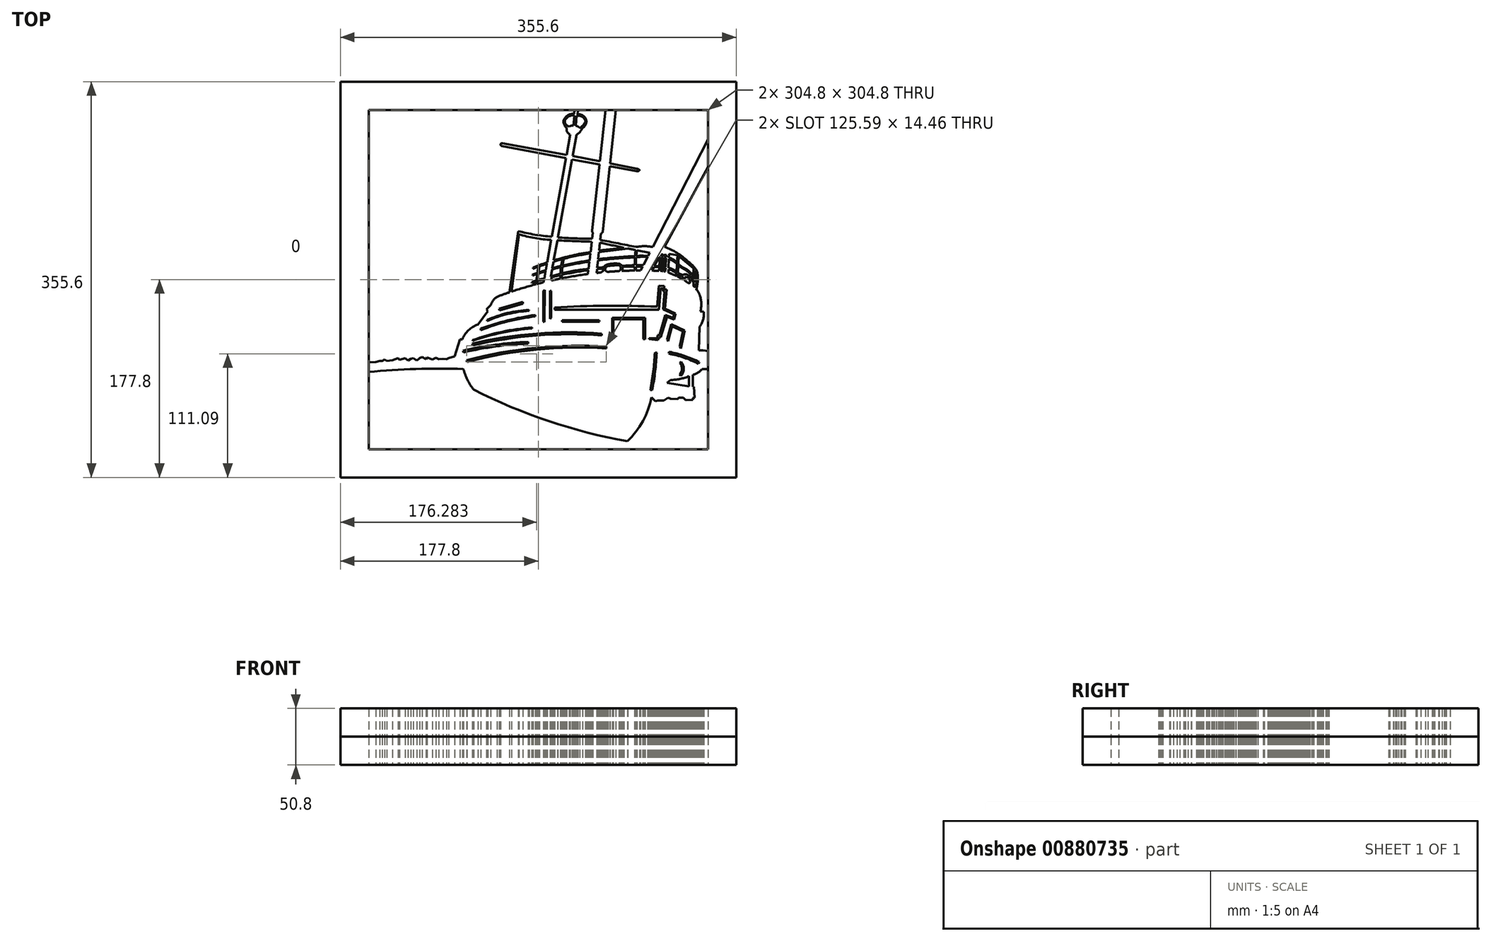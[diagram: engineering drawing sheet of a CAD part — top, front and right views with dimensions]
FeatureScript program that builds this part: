
annotation { "Feature Type Name" : "Feature", "Feature Type Description" : "" }
export const myFeature = defineFeature(function(context is Context, id is Id, definition is map)
    precondition{}
    {
        {
            var Q0;
            Q0=qCreatedBy(makeId("Top.planeOp"),FACE);
            var sketch = newSketch(context, id + "F0", { "sketchPlane" : qUnion([Q0])});
            skLineSegment(sketch, "E0.bottom", {"start": v(0, 0) * mm, "end": v(304.8, 0) * mm});
            skLineSegment(sketch, "E0.top", {"start": v(0, 304.8) * mm, "end": v(304.8, 304.8) * mm});
            skLineSegment(sketch, "E0.left", {"start": v(0, 0) * mm, "end": v(0, 304.8) * mm});
            skLineSegment(sketch, "E0.right", {"start": v(304.8, 0) * mm, "end": v(304.8, 304.8) * mm});
            skArc(sketch, "E1", {"start": v(94.3, 53.56) * mm, "mid": v(161.73, 25.31) * mm, "end": v(232.56, 7.17) * mm});
            skArc(sketch, "E2", {"start": v(85.05, 72.16) * mm, "mid": v(88.82, 62.44) * mm, "end": v(94.3, 53.56) * mm});
            skArc(sketch, "E3", {"start": v(232.56, 7.17) * mm, "mid": v(246.4, 25.26) * mm, "end": v(254.14, 46.67) * mm});
            skLineSegment(sketch, "E4", {"start": v(254.14, 46.67) * mm, "end": v(271.17, 62.17) * mm});
            skArc(sketch, "E5", {"start": v(271.17, 62.17) * mm, "mid": v(279.66, 63.15) * mm, "end": v(287.85, 65.57) * mm});
            skArc(sketch, "E6", {"start": v(290.4, 66.66) * mm, "mid": v(295.48, 68.46) * mm, "end": v(299.52, 72.01) * mm});
            skArc(sketch, "E7", {"start": v(297.32, 110.03) * mm, "mid": v(300.5, 116.32) * mm, "end": v(301.08, 123.34) * mm});
            skArc(sketch, "E8", {"start": v(298.13, 123.68) * mm, "mid": v(298.87, 130.77) * mm, "end": v(297.77, 137.83) * mm});
            skArc(sketch, "E9", {"start": v(297.77, 137.83) * mm, "mid": v(296.7, 140.32) * mm, "end": v(295.27, 142.62) * mm});
            skLineSegment(sketch, "E10", {"start": v(299.52, 72.01) * mm, "end": v(299.52, 79.67) * mm});
            skLineSegment(sketch, "E11", {"start": v(299.52, 79.67) * mm, "end": v(300.6, 88.72) * mm});
            skLineSegment(sketch, "E12", {"start": v(300.6, 88.72) * mm, "end": v(296.73, 88.72) * mm});
            skLineSegment(sketch, "E13", {"start": v(296.73, 88.72) * mm, "end": v(297.32, 110.03) * mm});
            skLineSegment(sketch, "E14", {"start": v(301.08, 123.34) * mm, "end": v(298.13, 123.68) * mm});
            skLineSegment(sketch, "E15", {"start": v(77.34, 83.42) * mm, "end": v(81.94, 98.75) * mm});
            skLineSegment(sketch, "E16", {"start": v(81.94, 98.75) * mm, "end": v(84.22, 98.75) * mm});
            skArc(sketch, "E17", {"start": v(98.1, 112.03) * mm, "mid": v(89.73, 106.89) * mm, "end": v(84.22, 98.75) * mm});
            skLineSegment(sketch, "E18", {"start": v(98.1, 112.03) * mm, "end": v(107.17, 124.2) * mm});
            skLineSegment(sketch, "E19", {"start": v(107.17, 124.2) * mm, "end": v(105.8, 125.59) * mm});
            skLineSegment(sketch, "E20", {"start": v(105.8, 125.59) * mm, "end": v(109.7, 129.49) * mm});
            skArc(sketch, "E21", {"start": v(115.26, 136.92) * mm, "mid": v(111.9, 133.63) * mm, "end": v(109.7, 129.49) * mm});
            skArc(sketch, "E22", {"start": v(265, 160.04) * mm, "mid": v(218.95, 159.65) * mm, "end": v(173.3, 153.51) * mm});
            skArc(sketch, "E23", {"start": v(295.27, 142.62) * mm, "mid": v(281.2, 153.19) * mm, "end": v(265, 160.04) * mm});
            skLineSegment(sketch, "E24", {"start": v(164.3, 151.6) * mm, "end": v(164.3, 154.55) * mm});
            skLineSegment(sketch, "E25", {"start": v(164.3, 154.55) * mm, "end": v(163.51, 154.41) * mm});
            skLineSegment(sketch, "E26", {"start": v(157.8, 153.4) * mm, "end": v(157.06, 149.9) * mm});
            skLineSegment(sketch, "E27", {"start": v(163.51, 154.41) * mm, "end": v(163.62, 155.02) * mm});
            skArc(sketch, "E28", {"start": v(186.7, 282.65) * mm, "mid": v(188.34, 283.6) * mm, "end": v(189.8, 284.83) * mm});
            skArc(sketch, "E29", {"start": v(192.3, 288.71) * mm, "mid": v(195.4, 292.6) * mm, "end": v(194.77, 297.54) * mm});
            skArc(sketch, "E30", {"start": v(194.77, 297.54) * mm, "mid": v(191.72, 300.14) * mm, "end": v(187.83, 301.08) * mm});
            skLineSegment(sketch, "E31", {"start": v(188.16, 304.8) * mm, "end": v(187.83, 301.08) * mm});
            skLineSegment(sketch, "E32", {"start": v(184.75, 301.25) * mm, "end": v(185.1, 304.78) * mm});
            skLineSegment(sketch, "E33", {"start": v(184.1, 290.76) * mm, "end": v(184.92, 299.78) * mm});
            skLineSegment(sketch, "E34", {"start": v(186.1, 290.67) * mm, "end": v(186.92, 299.5) * mm});
            skLineSegment(sketch, "E35", {"start": v(181.18, 282.83) * mm, "end": v(177.88, 264.54) * mm});
            skLineSegment(sketch, "E36", {"start": v(204.79, 158.37) * mm, "end": v(208.84, 193.9) * mm});
            skLineSegment(sketch, "E37", {"start": v(201.6, 194.48) * mm, "end": v(197, 157.43) * mm});
            skLineSegment(sketch, "E38", {"start": v(210.44, 195.17) * mm, "end": v(216.63, 254.16) * mm});
            skLineSegment(sketch, "E39", {"start": v(212.83, 304.8) * mm, "end": v(200.7, 196.5) * mm});
            skArc(sketch, "E40", {"start": v(200.7, 196.5) * mm, "mid": v(200.87, 195.36) * mm, "end": v(201.6, 194.48) * mm});
            skArc(sketch, "E41", {"start": v(208.84, 193.9) * mm, "mid": v(209.71, 194.44) * mm, "end": v(210.44, 195.17) * mm});
            skArc(sketch, "E42", {"start": v(134.37, 196) * mm, "mid": v(149.36, 192.78) * mm, "end": v(164.59, 190.94) * mm});
            skArc(sketch, "E43", {"start": v(135.06, 193.07) * mm, "mid": v(149.41, 189.7) * mm, "end": v(164.07, 188.09) * mm});
            skArc(sketch, "E44", {"start": v(169.98, 190.2) * mm, "mid": v(185.45, 189.43) * mm, "end": v(200.92, 189.03) * mm});
            skArc(sketch, "E45", {"start": v(169.53, 187.72) * mm, "mid": v(185.07, 186.99) * mm, "end": v(200.6, 186.47) * mm});
            skArc(sketch, "E46", {"start": v(208.18, 188.12) * mm, "mid": v(224.23, 184.9) * mm, "end": v(240.3, 181.72) * mm});
            skArc(sketch, "E47", {"start": v(207.88, 185.56) * mm, "mid": v(218.64, 183.28) * mm, "end": v(229.41, 181.06) * mm});
            skLineSegment(sketch, "E48", {"start": v(244.44, 160.58) * mm, "end": v(304.8, 278.4) * mm});
            skLineSegment(sketch, "E49", {"start": v(304.8, 253.65) * mm, "end": v(254.47, 160.46) * mm});
            skLineSegment(sketch, "E50", {"start": v(119.8, 272.39) * mm, "end": v(177.33, 261.5) * mm});
            skLineSegment(sketch, "E51", {"start": v(177.88, 264.54) * mm, "end": v(120.16, 274.96) * mm});
            skLineSegment(sketch, "E52", {"start": v(182.65, 260.3) * mm, "end": v(207.34, 255.83) * mm});
            skLineSegment(sketch, "E53", {"start": v(183.2, 263.37) * mm, "end": v(207.65, 258.6) * mm});
            skArc(sketch, "E54", {"start": v(177.98, 288.57) * mm, "mid": v(178.4, 285.04) * mm, "end": v(181.18, 282.83) * mm});
            skArc(sketch, "E55", {"start": v(189.8, 284.83) * mm, "mid": v(191.13, 286.72) * mm, "end": v(192.3, 288.71) * mm});
            skArc(sketch, "E56", {"start": v(184.92, 299.78) * mm, "mid": v(179.69, 298.94) * mm, "end": v(176.25, 294.92) * mm});
            skArc(sketch, "E57", {"start": v(194.86, 294.45) * mm, "mid": v(191.95, 298.64) * mm, "end": v(186.92, 299.5) * mm});
            skArc(sketch, "E58", {"start": v(189.8, 288.71) * mm, "mid": v(192.76, 291.2) * mm, "end": v(194.86, 294.45) * mm});
            skArc(sketch, "E59", {"start": v(176.25, 294.92) * mm, "mid": v(177.3, 291.63) * mm, "end": v(180.28, 289.9) * mm});
            skArc(sketch, "E60", {"start": v(184.1, 290.76) * mm, "mid": v(182.11, 290.65) * mm, "end": v(180.28, 289.9) * mm});
            skArc(sketch, "E61", {"start": v(189.8, 288.71) * mm, "mid": v(188.07, 289.93) * mm, "end": v(186.1, 290.67) * mm});
            skArc(sketch, "E62", {"start": v(120.16, 274.96) * mm, "mid": v(119.17, 274.8) * mm, "end": v(118.5, 274.06) * mm});
            skArc(sketch, "E63", {"start": v(118.5, 274.06) * mm, "mid": v(118.83, 272.98) * mm, "end": v(119.8, 272.39) * mm});
            skArc(sketch, "E64", {"start": v(243.5, 250.67) * mm, "mid": v(242.29, 251.62) * mm, "end": v(240.83, 252.15) * mm});
            skArc(sketch, "E65", {"start": v(240.69, 249.81) * mm, "mid": v(242.2, 249.9) * mm, "end": v(243.5, 250.67) * mm});
            skArc(sketch, "E66", {"start": v(199.46, 177.22) * mm, "mid": v(182.73, 174.03) * mm, "end": v(166.27, 169.67) * mm});
            skArc(sketch, "E67", {"start": v(199.3, 175.95) * mm, "mid": v(187.26, 173.85) * mm, "end": v(175.35, 171.11) * mm});
            skArc(sketch, "E68", {"start": v(198.51, 169.56) * mm, "mid": v(186.36, 167.57) * mm, "end": v(174.32, 165) * mm});
            skArc(sketch, "E69", {"start": v(198.38, 168.5) * mm, "mid": v(186.23, 166.55) * mm, "end": v(174.19, 164) * mm});
            skArc(sketch, "E70", {"start": v(157.8, 153.4) * mm, "mid": v(154.81, 152.78) * mm, "end": v(151.86, 152) * mm});
            skArc(sketch, "E71", {"start": v(157.6, 152.46) * mm, "mid": v(154.66, 151.92) * mm, "end": v(151.76, 151.15) * mm});
            skArc(sketch, "E72", {"start": v(197.57, 161.96) * mm, "mid": v(185.48, 160.45) * mm, "end": v(173.56, 157.93) * mm});
            skArc(sketch, "E73", {"start": v(197.44, 160.93) * mm, "mid": v(185.42, 159.02) * mm, "end": v(173.47, 156.67) * mm});
            skArc(sketch, "E74", {"start": v(175.35, 171.11) * mm, "mid": v(174.26, 164.55) * mm, "end": v(173.56, 157.93) * mm});
            skArc(sketch, "E75", {"start": v(174.15, 170.8) * mm, "mid": v(172.97, 164.24) * mm, "end": v(172.34, 157.62) * mm});
            skLineSegment(sketch, "E76", {"start": v(207.1, 178.6) * mm, "end": v(229.41, 181.06) * mm});
            skLineSegment(sketch, "E77", {"start": v(232.84, 180.37) * mm, "end": v(206.93, 177.2) * mm});
            skArc(sketch, "E78", {"start": v(239.54, 173.56) * mm, "mid": v(222.85, 172.45) * mm, "end": v(206.2, 170.79) * mm});
            skArc(sketch, "E79", {"start": v(239.13, 172.33) * mm, "mid": v(222.57, 171.35) * mm, "end": v(206.07, 169.65) * mm});
            skArc(sketch, "E80", {"start": v(251.1, 173.56) * mm, "mid": v(245.8, 173.79) * mm, "end": v(240.49, 173.63) * mm});
            skArc(sketch, "E81", {"start": v(250.73, 172.86) * mm, "mid": v(245.55, 172.9) * mm, "end": v(240.39, 172.5) * mm});
            skArc(sketch, "E82", {"start": v(239.92, 178.96) * mm, "mid": v(239.63, 176.26) * mm, "end": v(239.4, 173.56) * mm});
            skArc(sketch, "E83", {"start": v(241.08, 178.6) * mm, "mid": v(240.75, 176.12) * mm, "end": v(240.49, 173.63) * mm});
            skArc(sketch, "E84", {"start": v(227.38, 160.16) * mm, "mid": v(228.04, 163.87) * mm, "end": v(225.37, 166.53) * mm});
            skArc(sketch, "E85", {"start": v(225.37, 166.53) * mm, "mid": v(219.91, 166.77) * mm, "end": v(214.51, 165.95) * mm});
            skArc(sketch, "E86", {"start": v(214.51, 165.95) * mm, "mid": v(211.53, 163.92) * mm, "end": v(210.83, 160.38) * mm});
            skArc(sketch, "E87", {"start": v(212.7, 160.6) * mm, "mid": v(213.91, 159.64) * mm, "end": v(215.44, 159.39) * mm});
            skArc(sketch, "E88", {"start": v(214.95, 164.65) * mm, "mid": v(212.98, 163.1) * mm, "end": v(212.7, 160.6) * mm});
            skArc(sketch, "E89", {"start": v(225.08, 165.3) * mm, "mid": v(220, 165.13) * mm, "end": v(214.95, 164.65) * mm});
            skArc(sketch, "E90", {"start": v(225.08, 160.04) * mm, "mid": v(226.54, 162.67) * mm, "end": v(225.08, 165.3) * mm});
            skArc(sketch, "E91", {"start": v(208.2, 158.73) * mm, "mid": v(209.65, 159.34) * mm, "end": v(210.83, 160.38) * mm});
            skArc(sketch, "E92", {"start": v(210.83, 162.18) * mm, "mid": v(208, 162.17) * mm, "end": v(205.2, 161.9) * mm});
            skArc(sketch, "E93", {"start": v(211.22, 163.37) * mm, "mid": v(208.27, 163.22) * mm, "end": v(205.32, 163) * mm});
            skArc(sketch, "E94", {"start": v(239.06, 165.3) * mm, "mid": v(233.38, 165.04) * mm, "end": v(227.7, 164.65) * mm});
            skArc(sketch, "E95", {"start": v(239.06, 164.25) * mm, "mid": v(233.55, 164.14) * mm, "end": v(228.04, 163.87) * mm});
            skArc(sketch, "E96", {"start": v(255.27, 181.72) * mm, "mid": v(247.78, 182.4) * mm, "end": v(240.3, 181.72) * mm});
            skArc(sketch, "E97", {"start": v(295.37, 159.35) * mm, "mid": v(291.54, 164.64) * mm, "end": v(286.66, 168.96) * mm});
            skArc(sketch, "E98", {"start": v(294.43, 143.41) * mm, "mid": v(295.67, 151.34) * mm, "end": v(295.37, 159.35) * mm});
            skLineSegment(sketch, "E99", {"start": v(240.08, 165.4) * mm, "end": v(247, 165.6) * mm});
            skLineSegment(sketch, "E100", {"start": v(240.08, 164.1) * mm, "end": v(246.25, 164.1) * mm});
            skLineSegment(sketch, "E101", {"start": v(260.92, 160.24) * mm, "end": v(261.62, 172.53) * mm});
            skLineSegment(sketch, "E102", {"start": v(262.22, 160.18) * mm, "end": v(262.93, 172.5) * mm});
            skLineSegment(sketch, "E103", {"start": v(263.06, 174.8) * mm, "end": v(264.68, 175.25) * mm});
            skLineSegment(sketch, "E104", {"start": v(264.68, 175.25) * mm, "end": v(264.18, 160.09) * mm});
            skLineSegment(sketch, "E105", {"start": v(265, 160.04) * mm, "end": v(265.54, 174.62) * mm});
            skLineSegment(sketch, "E106", {"start": v(265.54, 174.62) * mm, "end": v(267.47, 174.55) * mm});
            skLineSegment(sketch, "E107", {"start": v(269.35, 158.65) * mm, "end": v(269.92, 175.49) * mm});
            skLineSegment(sketch, "E108", {"start": v(269.92, 175.49) * mm, "end": v(277.52, 174.4) * mm});
            skLineSegment(sketch, "E109", {"start": v(277.52, 174.4) * mm, "end": v(276.33, 155.75) * mm});
            skLineSegment(sketch, "E110", {"start": v(277.65, 155.1) * mm, "end": v(278.7, 173.55) * mm});
            skLineSegment(sketch, "E111", {"start": v(278.7, 173.55) * mm, "end": v(292.02, 162.47) * mm});
            skLineSegment(sketch, "E112", {"start": v(292.02, 162.47) * mm, "end": v(291.2, 150.99) * mm});
            skLineSegment(sketch, "E113", {"start": v(291.2, 150.99) * mm, "end": v(290.35, 151.05) * mm});
            skLineSegment(sketch, "E114", {"start": v(292.02, 146.61) * mm, "end": v(292.8, 160.42) * mm});
            skLineSegment(sketch, "E115", {"start": v(292.8, 160.42) * mm, "end": v(294.61, 158.05) * mm});
            skLineSegment(sketch, "E116", {"start": v(294.61, 158.05) * mm, "end": v(294.61, 152.4) * mm});
            skLineSegment(sketch, "E117", {"start": v(294.61, 152.4) * mm, "end": v(292.48, 154.95) * mm});
            skLineSegment(sketch, "E118", {"start": v(282.2, 152.6) * mm, "end": v(282.2, 155.15) * mm});
            skLineSegment(sketch, "E119", {"start": v(282.2, 155.15) * mm, "end": v(277.77, 157.25) * mm});
            skLineSegment(sketch, "E120", {"start": v(277.84, 158.44) * mm, "end": v(282.14, 156.42) * mm});
            skLineSegment(sketch, "E121", {"start": v(256.22, 163.7) * mm, "end": v(261.1, 163.42) * mm});
            skLineSegment(sketch, "E122", {"start": v(261.16, 164.33) * mm, "end": v(256.7, 164.58) * mm});
            skLineSegment(sketch, "E123", {"start": v(262.4, 163.3) * mm, "end": v(264.28, 163.24) * mm});
            skLineSegment(sketch, "E124", {"start": v(262.46, 164.31) * mm, "end": v(264.31, 164.25) * mm});
            skLineSegment(sketch, "E125", {"start": v(265.15, 164.1) * mm, "end": v(266.84, 163.74) * mm});
            skLineSegment(sketch, "E126", {"start": v(266.78, 162.74) * mm, "end": v(265.12, 163.14) * mm});
            skLineSegment(sketch, "E127", {"start": v(261.13, 172.8) * mm, "end": v(261.62, 172.53) * mm});
            skLineSegment(sketch, "E128", {"start": v(262.93, 172.5) * mm, "end": v(264.58, 172.4) * mm});
            skLineSegment(sketch, "E129", {"start": v(262.97, 173.3) * mm, "end": v(264.61, 173.25) * mm});
            skLineSegment(sketch, "E130", {"start": v(267.31, 171.78) * mm, "end": v(265.45, 172.21) * mm});
            skLineSegment(sketch, "E131", {"start": v(267.36, 172.57) * mm, "end": v(265.48, 173.04) * mm});
            skLineSegment(sketch, "E132", {"start": v(252.6, 176.52) * mm, "end": v(241.08, 178.6) * mm});
            skArc(sketch, "E133", {"start": v(277.1, 167.84) * mm, "mid": v(273.75, 170.45) * mm, "end": v(269.8, 172.04) * mm});
            skArc(sketch, "E134", {"start": v(277.01, 166.46) * mm, "mid": v(273.63, 169.1) * mm, "end": v(269.77, 170.95) * mm});
            skArc(sketch, "E135", {"start": v(276.55, 159.18) * mm, "mid": v(273.34, 161.65) * mm, "end": v(269.5, 162.91) * mm});
            skArc(sketch, "E136", {"start": v(276.46, 157.85) * mm, "mid": v(273.23, 160.26) * mm, "end": v(269.45, 161.65) * mm});
            skArc(sketch, "E137", {"start": v(285.67, 157.17) * mm, "mid": v(283.85, 157.09) * mm, "end": v(282.14, 156.42) * mm});
            skArc(sketch, "E138", {"start": v(290.1, 153.5) * mm, "mid": v(288.1, 155.6) * mm, "end": v(285.67, 157.17) * mm});
            skArc(sketch, "E139", {"start": v(290.35, 151.05) * mm, "mid": v(290.47, 152.3) * mm, "end": v(290.1, 153.5) * mm});
            skArc(sketch, "E140", {"start": v(288.57, 151.94) * mm, "mid": v(286.83, 154.14) * mm, "end": v(284.06, 154.54) * mm});
            skArc(sketch, "E141", {"start": v(288.57, 149.43) * mm, "mid": v(288.7, 150.69) * mm, "end": v(288.57, 151.94) * mm});
            skArc(sketch, "E142", {"start": v(284.06, 154.54) * mm, "mid": v(283.83, 153) * mm, "end": v(284.06, 151.46) * mm});
            skArc(sketch, "E143", {"start": v(287.06, 149.43) * mm, "mid": v(287.81, 149.3) * mm, "end": v(288.57, 149.43) * mm});
            skArc(sketch, "E144", {"start": v(292.02, 146.61) * mm, "mid": v(292.63, 145.96) * mm, "end": v(293.53, 145.92) * mm});
            skArc(sketch, "E145", {"start": v(293.53, 145.92) * mm, "mid": v(294.27, 148.46) * mm, "end": v(294.38, 151.1) * mm});
            skArc(sketch, "E146", {"start": v(294.38, 151.1) * mm, "mid": v(293.47, 152.23) * mm, "end": v(292.39, 153.19) * mm});
            skArc(sketch, "E147", {"start": v(291.55, 155.97) * mm, "mid": v(287.64, 160.14) * mm, "end": v(282.78, 163.13) * mm});
            skArc(sketch, "E148", {"start": v(291.47, 154.88) * mm, "mid": v(287.42, 159.03) * mm, "end": v(282.62, 162.27) * mm});
            skArc(sketch, "E149", {"start": v(278.25, 165.49) * mm, "mid": v(280.3, 163.7) * mm, "end": v(282.62, 162.27) * mm});
            skArc(sketch, "E150", {"start": v(278.3, 166.52) * mm, "mid": v(280.41, 164.66) * mm, "end": v(282.78, 163.13) * mm});
            skArc(sketch, "E151.trimOffspring", {"start": v(286.66, 168.96) * mm, "mid": v(276.97, 176.42) * mm, "end": v(265.95, 181.72) * mm});
            skArc(sketch, "E152", {"start": v(153.46, 164.32) * mm, "mid": v(153.08, 161.55) * mm, "end": v(152.72, 158.79) * mm});
            skArc(sketch, "E153", {"start": v(150.3, 148.17) * mm, "mid": v(150.48, 149.48) * mm, "end": v(150.66, 150.8) * mm});
            skLineSegment(sketch, "E154", {"start": v(135.06, 193.07) * mm, "end": v(128.56, 141.65) * mm});
            skLineSegment(sketch, "E155", {"start": v(134.37, 196) * mm, "end": v(126.49, 140.95) * mm});
            skLineSegment(sketch, "E156", {"start": v(146.54, 150.1) * mm, "end": v(146.97, 149.3) * mm});
            skLineSegment(sketch, "E157", {"start": v(147.54, 156.1) * mm, "end": v(147.2, 156.86) * mm});
            skLineSegment(sketch, "E158", {"start": v(147.7, 163.23) * mm, "end": v(147.92, 162.22) * mm});
            skPoint(sketch, "E159", {"position": v(180.34, 295.78) * mm});
            skPoint(sketch, "E160", {"position": v(182.6, 295.72) * mm});
            skLineSegment(sketch, "E161", {"start": v(0.01, 78.06) * mm, "end": v(6.4, 78.42) * mm});
            skLineSegment(sketch, "E162", {"start": v(6.4, 78.42) * mm, "end": v(10.04, 79.33) * mm});
            skLineSegment(sketch, "E163", {"start": v(10.04, 79.33) * mm, "end": v(12.22, 79.33) * mm});
            skLineSegment(sketch, "E164", {"start": v(12.22, 79.33) * mm, "end": v(14.41, 80.6) * mm});
            skLineSegment(sketch, "E165", {"start": v(14.41, 80.6) * mm, "end": v(16.42, 79.33) * mm});
            skLineSegment(sketch, "E166", {"start": v(16.42, 79.33) * mm, "end": v(21.34, 79.88) * mm});
            skLineSegment(sketch, "E167", {"start": v(21.34, 79.88) * mm, "end": v(26.44, 81.7) * mm});
            skLineSegment(sketch, "E168", {"start": v(26.44, 81.7) * mm, "end": v(27.72, 80.24) * mm});
            skLineSegment(sketch, "E169", {"start": v(27.72, 80.24) * mm, "end": v(32.82, 81.88) * mm});
            skLineSegment(sketch, "E170", {"start": v(32.82, 81.88) * mm, "end": v(35.56, 79.7) * mm});
            skLineSegment(sketch, "E171", {"start": v(35.56, 79.7) * mm, "end": v(37.93, 81.34) * mm});
            skLineSegment(sketch, "E172", {"start": v(37.93, 81.34) * mm, "end": v(40.11, 81.88) * mm});
            skLineSegment(sketch, "E173", {"start": v(40.11, 81.88) * mm, "end": v(43.21, 79.7) * mm});
            skLineSegment(sketch, "E174", {"start": v(43.21, 79.7) * mm, "end": v(45.95, 81.88) * mm});
            skLineSegment(sketch, "E175", {"start": v(45.95, 81.88) * mm, "end": v(48.14, 82.8) * mm});
            skLineSegment(sketch, "E176", {"start": v(48.14, 82.8) * mm, "end": v(51.6, 80.8) * mm});
            skLineSegment(sketch, "E177", {"start": v(51.6, 80.8) * mm, "end": v(52.7, 82.61) * mm});
            skLineSegment(sketch, "E178", {"start": v(52.7, 82.61) * mm, "end": v(57.25, 80.6) * mm});
            skLineSegment(sketch, "E179", {"start": v(57.25, 80.6) * mm, "end": v(60.53, 82.25) * mm});
            skLineSegment(sketch, "E180", {"start": v(60.53, 82.25) * mm, "end": v(63.08, 80.8) * mm});
            skLineSegment(sketch, "E181", {"start": v(63.08, 80.8) * mm, "end": v(66.73, 81.16) * mm});
            skLineSegment(sketch, "E182", {"start": v(66.73, 81.16) * mm, "end": v(70.01, 80.8) * mm});
            skLineSegment(sketch, "E183", {"start": v(70.01, 80.8) * mm, "end": v(71.83, 81.88) * mm});
            skLineSegment(sketch, "E184", {"start": v(71.83, 81.88) * mm, "end": v(77.34, 83.42) * mm});
            skArc(sketch, "E185", {"start": v(85.05, 72.16) * mm, "mid": v(42.48, 72.07) * mm, "end": v(0, 69.4) * mm});
            skLineSegment(sketch, "E186", {"start": v(300.6, 88.72) * mm, "end": v(304.8, 88.22) * mm});
            skLineSegment(sketch, "E187", {"start": v(299.52, 72.01) * mm, "end": v(304.8, 72.01) * mm});
            skLineSegment(sketch, "E188", {"start": v(268.25, 59.52) * mm, "end": v(287.85, 56.39) * mm});
            skLineSegment(sketch, "E189", {"start": v(287.85, 56.39) * mm, "end": v(287.85, 65.57) * mm});
            skLineSegment(sketch, "E190", {"start": v(291.24, 66.81) * mm, "end": v(291.24, 56.28) * mm});
            skLineSegment(sketch, "E191", {"start": v(291.24, 56.28) * mm, "end": v(292.22, 56.28) * mm});
            skLineSegment(sketch, "E192", {"start": v(292.22, 56.28) * mm, "end": v(292.91, 46.4) * mm});
            skLineSegment(sketch, "E193", {"start": v(292.91, 46.4) * mm, "end": v(291.3, 46.06) * mm});
            skLineSegment(sketch, "E194", {"start": v(291.3, 46.06) * mm, "end": v(291.42, 44.34) * mm});
            skLineSegment(sketch, "E195", {"start": v(291.42, 44.34) * mm, "end": v(285.1, 44) * mm});
            skLineSegment(sketch, "E196", {"start": v(285.1, 44) * mm, "end": v(282.7, 46.18) * mm});
            skLineSegment(sketch, "E197", {"start": v(282.7, 46.18) * mm, "end": v(278.56, 46.3) * mm});
            skLineSegment(sketch, "E198", {"start": v(278.56, 46.3) * mm, "end": v(277.64, 45.14) * mm});
            skLineSegment(sketch, "E199", {"start": v(277.64, 45.14) * mm, "end": v(271.2, 45.49) * mm});
            skLineSegment(sketch, "E200", {"start": v(271.2, 45.49) * mm, "end": v(269.02, 46.3) * mm});
            skLineSegment(sketch, "E201", {"start": v(269.02, 46.3) * mm, "end": v(265.35, 43.76) * mm});
            skLineSegment(sketch, "E202", {"start": v(265.35, 43.76) * mm, "end": v(259.95, 43.65) * mm});
            skLineSegment(sketch, "E203", {"start": v(259.95, 43.65) * mm, "end": v(257.54, 43.07) * mm});
            skLineSegment(sketch, "E204", {"start": v(257.54, 43.07) * mm, "end": v(254.14, 46.67) * mm});
            skArc(sketch, "E205", {"start": v(213.68, 92.21) * mm, "mid": v(150.4, 91.12) * mm, "end": v(88.1, 80.06) * mm});
            skArc(sketch, "E206", {"start": v(254.77, 52.86) * mm, "mid": v(257.4, 69.71) * mm, "end": v(258.82, 86.71) * mm});
            skArc(sketch, "E207", {"start": v(296.43, 76.87) * mm, "mid": v(283.42, 82.24) * mm, "end": v(269.81, 85.85) * mm});
            skLineSegment(sketch, "E208", {"start": v(218.88, 102.92) * mm, "end": v(218.88, 117.96) * mm});
            skLineSegment(sketch, "E209", {"start": v(218.88, 117.96) * mm, "end": v(248.4, 117.96) * mm});
            skLineSegment(sketch, "E210", {"start": v(248.4, 117.96) * mm, "end": v(248.4, 98.58) * mm});
            skLineSegment(sketch, "E211", {"start": v(280.52, 90.47) * mm, "end": v(284, 106.68) * mm});
            skLineSegment(sketch, "E212", {"start": v(284, 106.68) * mm, "end": v(271.84, 112.47) * mm});
            skLineSegment(sketch, "E213", {"start": v(271.84, 112.47) * mm, "end": v(268.08, 98.29) * mm});
            skArc(sketch, "E214", {"start": v(143.36, 94.82) * mm, "mid": v(114.1, 92.27) * mm, "end": v(85.2, 87) * mm});
            skArc(sketch, "E215", {"start": v(294.12, 85.27) * mm, "mid": v(291.4, 86.95) * mm, "end": v(288.27, 87.58) * mm});
            skArc(sketch, "E216", {"start": v(279.31, 67.12) * mm, "mid": v(281.48, 72.3) * mm, "end": v(279.46, 77.53) * mm});
            skArc(sketch, "E217", {"start": v(209.3, 102.23) * mm, "mid": v(151.08, 102.16) * mm, "end": v(93.54, 93.28) * mm});
            skArc(sketch, "E218", {"start": v(259.35, 128.12) * mm, "mid": v(213.24, 128.86) * mm, "end": v(167.14, 127.4) * mm});
            skLineSegment(sketch, "E219", {"start": v(259.35, 128.12) * mm, "end": v(260.97, 146.99) * mm});
            skLineSegment(sketch, "E220", {"start": v(260.97, 146.99) * mm, "end": v(265.59, 146.59) * mm});
            skLineSegment(sketch, "E221", {"start": v(265.59, 146.59) * mm, "end": v(265.6, 143.38) * mm});
            skLineSegment(sketch, "E222", {"start": v(265.6, 143.38) * mm, "end": v(267.7, 143.38) * mm});
            skLineSegment(sketch, "E223", {"start": v(267.7, 143.38) * mm, "end": v(266.33, 126.33) * mm});
            skLineSegment(sketch, "E224", {"start": v(217.43, 129.02) * mm, "end": v(217.43, 130.46) * mm});
            skLineSegment(sketch, "E225", {"start": v(217.43, 130.46) * mm, "end": v(193.85, 132.63) * mm});
            skLineSegment(sketch, "E226", {"start": v(193.85, 132.63) * mm, "end": v(192.54, 130.6) * mm});
            skLineSegment(sketch, "E227", {"start": v(192.54, 130.6) * mm, "end": v(194.28, 128.58) * mm});
            skLineSegment(sketch, "E228", {"start": v(156.95, 114.55) * mm, "end": v(156.95, 142.18) * mm});
            skLineSegment(sketch, "E229", {"start": v(163.9, 142.18) * mm, "end": v(163.9, 118.16) * mm});
            skLineSegment(sketch, "E230", {"start": v(218.88, 102.92) * mm, "end": v(219.94, 102.5) * mm});
            skLineSegment(sketch, "E231", {"start": v(219.94, 102.5) * mm, "end": v(219.94, 116.82) * mm});
            skLineSegment(sketch, "E232", {"start": v(219.94, 116.82) * mm, "end": v(246.94, 116.55) * mm});
            skLineSegment(sketch, "E233", {"start": v(246.94, 116.55) * mm, "end": v(246.94, 98.87) * mm});
            skLineSegment(sketch, "E234", {"start": v(246.94, 98.87) * mm, "end": v(248.4, 98.58) * mm});
            skLineSegment(sketch, "E235", {"start": v(268.08, 98.29) * mm, "end": v(268.94, 97.2) * mm});
            skLineSegment(sketch, "E236", {"start": v(268.94, 97.2) * mm, "end": v(272.49, 110.58) * mm});
            skLineSegment(sketch, "E237", {"start": v(272.49, 110.58) * mm, "end": v(282.3, 105.9) * mm});
            skLineSegment(sketch, "E238", {"start": v(282.3, 105.9) * mm, "end": v(279.56, 92.44) * mm});
            skLineSegment(sketch, "E239", {"start": v(279.56, 92.44) * mm, "end": v(280.52, 90.47) * mm});
            skArc(sketch, "E240.0", {"start": v(213.57, 90.56) * mm, "mid": v(150.56, 89.48) * mm, "end": v(88.5, 78.46) * mm});
            skArc(sketch, "E241.0", {"start": v(209.42, 103.88) * mm, "mid": v(150.95, 103.8) * mm, "end": v(93.17, 94.88) * mm});
            skArc(sketch, "E242.0", {"start": v(297.16, 78.36) * mm, "mid": v(283.95, 83.8) * mm, "end": v(270.13, 87.47) * mm});
            skArc(sketch, "E243.0", {"start": v(280.49, 65.96) * mm, "mid": v(283.13, 72.27) * mm, "end": v(280.66, 78.66) * mm});
            skArc(sketch, "E244.0", {"start": v(143.3, 96.47) * mm, "mid": v(113.88, 93.9) * mm, "end": v(84.83, 88.61) * mm});
            skLineSegment(sketch, "E245", {"start": v(143.36, 94.82) * mm, "end": v(143.3, 96.47) * mm});
            skLineSegment(sketch, "E246", {"start": v(93.54, 93.28) * mm, "end": v(93.17, 94.88) * mm});
            skLineSegment(sketch, "E247", {"start": v(85.2, 87) * mm, "end": v(84.83, 88.61) * mm});
            skLineSegment(sketch, "E248", {"start": v(88.5, 78.46) * mm, "end": v(88.1, 80.06) * mm});
            skLineSegment(sketch, "E249", {"start": v(213.57, 90.56) * mm, "end": v(213.68, 92.21) * mm});
            skLineSegment(sketch, "E250", {"start": v(209.3, 102.23) * mm, "end": v(209.42, 103.88) * mm});
            skLineSegment(sketch, "E251", {"start": v(269.81, 85.85) * mm, "end": v(270.13, 87.47) * mm});
            skLineSegment(sketch, "E252", {"start": v(296.43, 76.87) * mm, "end": v(297.16, 78.36) * mm});
            skLineSegment(sketch, "E253", {"start": v(279.46, 77.53) * mm, "end": v(280.66, 78.66) * mm});
            skLineSegment(sketch, "E254", {"start": v(279.31, 67.12) * mm, "end": v(280.49, 65.96) * mm});
            skArc(sketch, "E255.0", {"start": v(253.14, 53.17) * mm, "mid": v(255.77, 69.9) * mm, "end": v(257.17, 86.79) * mm});
            skLineSegment(sketch, "E256", {"start": v(258.82, 86.71) * mm, "end": v(257.17, 86.79) * mm});
            skLineSegment(sketch, "E257", {"start": v(254.77, 52.86) * mm, "end": v(253.14, 53.17) * mm});
            skLineSegment(sketch, "E258", {"start": v(252, 99.01) * mm, "end": v(259.7, 98.04) * mm});
            skLineSegment(sketch, "E259", {"start": v(259.7, 98.04) * mm, "end": v(261.07, 100.62) * mm});
            skLineSegment(sketch, "E260", {"start": v(261.07, 100.62) * mm, "end": v(262.56, 100.5) * mm});
            skLineSegment(sketch, "E261", {"start": v(262.56, 100.5) * mm, "end": v(268.19, 118.88) * mm});
            skLineSegment(sketch, "E262", {"start": v(268.19, 118.88) * mm, "end": v(274.62, 116.55) * mm});
            skLineSegment(sketch, "E263", {"start": v(274.62, 116.55) * mm, "end": v(275.77, 121.98) * mm});
            skLineSegment(sketch, "E264", {"start": v(275.77, 121.98) * mm, "end": v(266.33, 126.33) * mm});
            skLineSegment(sketch, "E265", {"start": v(138.65, 132.2) * mm, "end": v(117.3, 126.33) * mm});
            skLineSegment(sketch, "E266", {"start": v(117.3, 126.33) * mm, "end": v(117.7, 124.86) * mm});
            skLineSegment(sketch, "E267", {"start": v(117.7, 124.86) * mm, "end": v(138.65, 130.62) * mm});
            skLineSegment(sketch, "E268", {"start": v(138.65, 130.62) * mm, "end": v(138.65, 132.2) * mm});
            skLineSegment(sketch, "E269", {"start": v(167.14, 127.4) * mm, "end": v(167.14, 125.5) * mm});
            skLineSegment(sketch, "E270", {"start": v(167.14, 125.5) * mm, "end": v(260.97, 125.5) * mm});
            skLineSegment(sketch, "E271", {"start": v(260.97, 125.5) * mm, "end": v(262.42, 144.75) * mm});
            skLineSegment(sketch, "E272", {"start": v(262.42, 144.75) * mm, "end": v(264.44, 144.46) * mm});
            skLineSegment(sketch, "E273", {"start": v(264.44, 144.46) * mm, "end": v(264.59, 141.71) * mm});
            skLineSegment(sketch, "E274", {"start": v(264.59, 141.71) * mm, "end": v(265.89, 141.71) * mm});
            skLineSegment(sketch, "E275", {"start": v(265.89, 141.71) * mm, "end": v(264.73, 125.65) * mm});
            skLineSegment(sketch, "E276", {"start": v(264.73, 125.65) * mm, "end": v(274.42, 121.17) * mm});
            skLineSegment(sketch, "E277", {"start": v(274.42, 121.17) * mm, "end": v(273.56, 118.13) * mm});
            skLineSegment(sketch, "E278", {"start": v(273.56, 118.13) * mm, "end": v(266.47, 120.73) * mm});
            skLineSegment(sketch, "E279", {"start": v(266.47, 120.73) * mm, "end": v(261.55, 102.94) * mm});
            skLineSegment(sketch, "E280", {"start": v(261.55, 102.94) * mm, "end": v(259.96, 102.36) * mm});
            skLineSegment(sketch, "E281", {"start": v(259.96, 102.36) * mm, "end": v(259.23, 99.76) * mm});
            skLineSegment(sketch, "E282", {"start": v(259.23, 99.76) * mm, "end": v(252, 99.76) * mm});
            skLineSegment(sketch, "E283", {"start": v(252, 99.76) * mm, "end": v(252, 99.01) * mm});
            skLineSegment(sketch, "E284", {"start": v(173.87, 115.82) * mm, "end": v(207.3, 115.82) * mm});
            skLineSegment(sketch, "E285", {"start": v(207.3, 115.82) * mm, "end": v(207.36, 114.59) * mm});
            skLineSegment(sketch, "E286", {"start": v(207.36, 114.59) * mm, "end": v(173.87, 114.51) * mm});
            skLineSegment(sketch, "E287", {"start": v(173.87, 114.51) * mm, "end": v(173.87, 115.82) * mm});
            skArc(sketch, "E288", {"start": v(149.8, 120.57) * mm, "mid": v(125.03, 115.8) * mm, "end": v(100.9, 108.41) * mm});
            skArc(sketch, "E289", {"start": v(146.91, 109.42) * mm, "mid": v(119.84, 105.47) * mm, "end": v(93.52, 98) * mm});
            skArc(sketch, "E290", {"start": v(144.02, 125.2) * mm, "mid": v(124.87, 122.34) * mm, "end": v(106.54, 116.08) * mm});
            skArc(sketch, "E291", {"start": v(149.8, 119.28) * mm, "mid": v(124.95, 114.78) * mm, "end": v(100.9, 107.05) * mm});
            skArc(sketch, "E292", {"start": v(146.91, 108.41) * mm, "mid": v(119.88, 104.77) * mm, "end": v(93.62, 97.42) * mm});
            skLineSegment(sketch, "E293", {"start": v(93.62, 97.42) * mm, "end": v(93.52, 98) * mm});
            skLineSegment(sketch, "E294", {"start": v(100.9, 107.05) * mm, "end": v(100.9, 108.41) * mm});
            skLineSegment(sketch, "E295", {"start": v(146.91, 108.41) * mm, "end": v(146.91, 109.42) * mm});
            skLineSegment(sketch, "E296", {"start": v(149.8, 119.28) * mm, "end": v(149.8, 120.57) * mm});
            skArc(sketch, "E297", {"start": v(144.2, 124.25) * mm, "mid": v(124.9, 121.46) * mm, "end": v(106.44, 115.2) * mm});
            skLineSegment(sketch, "E298", {"start": v(106.44, 115.2) * mm, "end": v(106.54, 116.08) * mm});
            skLineSegment(sketch, "E299", {"start": v(144.2, 124.25) * mm, "end": v(144.02, 125.2) * mm});
            skLineSegment(sketch, "E300", {"start": v(156.95, 114.55) * mm, "end": v(157.98, 114.36) * mm});
            skLineSegment(sketch, "E301", {"start": v(157.98, 114.36) * mm, "end": v(158.13, 143.02) * mm});
            skLineSegment(sketch, "E302", {"start": v(158.13, 143.02) * mm, "end": v(156.95, 142.18) * mm});
            skLineSegment(sketch, "E303", {"start": v(163.9, 142.18) * mm, "end": v(162.97, 142.35) * mm});
            skLineSegment(sketch, "E304", {"start": v(162.97, 142.35) * mm, "end": v(162.97, 117.04) * mm});
            skLineSegment(sketch, "E305", {"start": v(162.97, 117.04) * mm, "end": v(163.9, 118.16) * mm});
            skLineSegment(sketch, "E306.bottom", {"start": v(-25.4, 330.2) * mm, "end": v(330.2, 330.2) * mm});
            skLineSegment(sketch, "E306.top", {"start": v(-25.4, -25.4) * mm, "end": v(330.2, -25.4) * mm});
            skLineSegment(sketch, "E306.left", {"start": v(-25.4, 330.2) * mm, "end": v(-25.4, -25.4) * mm});
            skLineSegment(sketch, "E306.right", {"start": v(330.2, 330.2) * mm, "end": v(330.2, -25.4) * mm});
            skArc(sketch, "E307.trimOffspring", {"start": v(157.06, 149.9) * mm, "mid": v(154.25, 149.2) * mm, "end": v(151.43, 148.47) * mm});
            skArc(sketch, "E308.trimOffspring", {"start": v(158.98, 159.89) * mm, "mid": v(155.78, 158.9) * mm, "end": v(152.6, 157.86) * mm});
            skArc(sketch, "E309.trimOffspring", {"start": v(159.15, 160.85) * mm, "mid": v(155.93, 159.84) * mm, "end": v(152.72, 158.79) * mm});
            skArc(sketch, "E310.trimOffspring", {"start": v(160.2, 166.66) * mm, "mid": v(156.82, 165.52) * mm, "end": v(153.46, 164.32) * mm});
            skArc(sketch, "E311.trimOffspring", {"start": v(160.4, 167.82) * mm, "mid": v(154.02, 165.61) * mm, "end": v(147.7, 163.23) * mm});
            skArc(sketch, "E312.trimOffspring", {"start": v(152.4, 163.93) * mm, "mid": v(150.16, 163.08) * mm, "end": v(147.92, 162.22) * mm});
            skArc(sketch, "E313.trimOffspring", {"start": v(151.68, 158.44) * mm, "mid": v(149.43, 157.66) * mm, "end": v(147.2, 156.86) * mm});
            skArc(sketch, "E314.trimOffspring", {"start": v(151.56, 157.5) * mm, "mid": v(149.54, 156.82) * mm, "end": v(147.54, 156.1) * mm});
            skArc(sketch, "E315.trimOffspring", {"start": v(152.6, 157.86) * mm, "mid": v(152.22, 154.93) * mm, "end": v(151.86, 152) * mm});
            skArc(sketch, "E316.trimOffspring", {"start": v(151.68, 158.44) * mm, "mid": v(152.04, 161.18) * mm, "end": v(152.4, 163.93) * mm});
            skArc(sketch, "E317.trimOffspring", {"start": v(151.76, 151.15) * mm, "mid": v(151.6, 149.8) * mm, "end": v(151.43, 148.47) * mm});
            skArc(sketch, "E318.trimOffspring", {"start": v(150.78, 151.66) * mm, "mid": v(148.64, 150.93) * mm, "end": v(146.54, 150.1) * mm});
            skArc(sketch, "E319.trimOffspring", {"start": v(150.78, 151.66) * mm, "mid": v(151.17, 154.58) * mm, "end": v(151.56, 157.5) * mm});
            skArc(sketch, "E320.trimOffspring", {"start": v(150.66, 150.8) * mm, "mid": v(148.8, 150.1) * mm, "end": v(146.97, 149.3) * mm});
            skArc(sketch, "E321.trimOffspring", {"start": v(150.3, 148.17) * mm, "mid": v(132.64, 142.98) * mm, "end": v(115.26, 136.92) * mm});
            skLineSegment(sketch, "E322.trimOffspring", {"start": v(164.99, 162.57) * mm, "end": v(169.53, 187.72) * mm});
            skArc(sketch, "E323.trimOffspring", {"start": v(174.15, 170.8) * mm, "mid": v(170.1, 169.7) * mm, "end": v(166.06, 168.52) * mm});
            skArc(sketch, "E324.trimOffspring", {"start": v(173.03, 164.68) * mm, "mid": v(169, 163.66) * mm, "end": v(164.99, 162.57) * mm});
            skArc(sketch, "E325.trimOffspring", {"start": v(172.9, 163.69) * mm, "mid": v(168.85, 162.67) * mm, "end": v(164.8, 161.58) * mm});
            skArc(sketch, "E326.trimOffspring", {"start": v(172.34, 157.62) * mm, "mid": v(167.96, 156.39) * mm, "end": v(163.62, 155.02) * mm});
            skArc(sketch, "E327.trimOffspring", {"start": v(172.29, 156.41) * mm, "mid": v(168.29, 155.5) * mm, "end": v(164.3, 154.55) * mm});
            skArc(sketch, "E328.trimOffspring", {"start": v(173.47, 156.67) * mm, "mid": v(173.38, 155.1) * mm, "end": v(173.3, 153.51) * mm});
            skArc(sketch, "E329.trimOffspring", {"start": v(172.29, 156.41) * mm, "mid": v(172.24, 154.85) * mm, "end": v(172.23, 153.3) * mm});
            skArc(sketch, "E330.trimOffspring", {"start": v(172.23, 153.3) * mm, "mid": v(168.26, 152.47) * mm, "end": v(164.3, 151.6) * mm});
            skLineSegment(sketch, "E331", {"start": v(164.8, 161.58) * mm, "end": v(163.62, 155.02) * mm});
            skArc(sketch, "E332.trimOffspring", {"start": v(232.84, 180.37) * mm, "mid": v(236.35, 179.67) * mm, "end": v(239.86, 178.97) * mm});
            skPoint(sketch, "E333.orphan", {"position": v(241.6, 181.72) * mm});
            skArc(sketch, "E334.extension", {"start": v(239.86, 178.97) * mm, "mid": v(239.9, 178.97) * mm, "end": v(239.92, 178.96) * mm});
            skArc(sketch, "E335.trimOffspring", {"start": v(240.39, 172.5) * mm, "mid": v(240.1, 166.53) * mm, "end": v(240.18, 160.55) * mm});
            skArc(sketch, "E336.trimOffspring", {"start": v(239.31, 172.36) * mm, "mid": v(239.07, 166.45) * mm, "end": v(239.13, 160.53) * mm});
            skArc(sketch, "E337.trimOffspring", {"start": v(239.31, 172.36) * mm, "mid": v(239.22, 172.34) * mm, "end": v(239.13, 172.33) * mm});
            skLineSegment(sketch, "E338.trimOffspring", {"start": v(262.97, 173.3) * mm, "end": v(263.06, 174.8) * mm});
            skLineSegment(sketch, "E339.trimOffspring", {"start": v(267.31, 171.78) * mm, "end": v(266.84, 163.74) * mm});
            skLineSegment(sketch, "E340.trimOffspring", {"start": v(266.78, 162.74) * mm, "end": v(266.6, 159.57) * mm});
            skLineSegment(sketch, "E341.trimOffspring", {"start": v(216.63, 254.16) * mm, "end": v(240.69, 249.81) * mm});
            skLineSegment(sketch, "E342.trimOffspring", {"start": v(216.9, 256.8) * mm, "end": v(240.83, 252.15) * mm});
            skLineSegment(sketch, "E343.trimOffspring", {"start": v(216.9, 256.8) * mm, "end": v(221.94, 304.8) * mm});
            skPoint(sketch, "E344.orphan", {"position": v(186.7, 301) * mm});
            skLineSegment(sketch, "E345.trimOffspring", {"start": v(183.2, 263.37) * mm, "end": v(186.7, 282.65) * mm});
            skLineSegment(sketch, "E346.trimOffspring", {"start": v(177.33, 261.5) * mm, "end": v(164.59, 190.94) * mm});
            skLineSegment(sketch, "E347.trimOffspring", {"start": v(164.07, 188.09) * mm, "end": v(157.8, 153.4) * mm});
            skLineSegment(sketch, "E348.trimOffspring", {"start": v(169.98, 190.2) * mm, "end": v(182.65, 260.3) * mm});
            skLineSegment(sketch, "E349", {"start": v(185.1, 304.78) * mm, "end": v(188.16, 304.8) * mm});
            skLineSegment(sketch, "E350", {"start": v(212.83, 304.8) * mm, "end": v(221.94, 304.8) * mm});
            skLineSegment(sketch, "E351", {"start": v(0, 69.4) * mm, "end": v(0.01, 78.06) * mm});
            skLineSegment(sketch, "E352", {"start": v(304.8, 72.01) * mm, "end": v(304.8, 88.22) * mm});
            skLineSegment(sketch, "E353", {"start": v(304.8, 253.65) * mm, "end": v(304.8, 278.4) * mm});
            skLineSegment(sketch, "E354.bottom", {"start": v(304.8, 304.8) * mm, "end": v(0, 304.8) * mm});
            skLineSegment(sketch, "E354.top", {"start": v(304.8, 0) * mm, "end": v(0, 0) * mm});
            skLineSegment(sketch, "E354.left", {"start": v(304.8, 304.8) * mm, "end": v(304.8, 0) * mm});
            skLineSegment(sketch, "E354.right", {"start": v(0, 304.8) * mm, "end": v(0, 0) * mm});
            skLineSegment(sketch, "E355", {"start": v(267.36, 172.57) * mm, "end": v(267.47, 174.55) * mm});
            skArc(sketch, "E356", {"start": v(175.1, 295.1) * mm, "mid": v(175.8, 291.51) * mm, "end": v(177.98, 288.57) * mm});
            skArc(sketch, "E357", {"start": v(184.76, 301.26) * mm, "mid": v(178.85, 299.87) * mm, "end": v(175.1, 295.1) * mm});
            skSolve(sketch);
        }
        {
            var Q0;
            Q0=makeQuery(id+"F0.imprint","IMPRINT",FACE,{"disambiguationData":[TD([[makeQuery(id+"F0.imprint","IMPRINT",EDGE,{"derivedFrom":sQuery(id+"F0.wireOp",EDGE,"E1")}),1.0]])]});
            var Q1;
            {var subQ3=sQuery(id+"F0.wireOp",EDGE,"E48");var subQ4=sQuery(id+"F0.wireOp",EDGE,"E22");var subQ5=makeQuery(id+"F0.imprint","INTERSECT",VERTEX,{"derivedFrom":[subQ4,subQ3]});Q1=makeQuery(id+"F0.imprint","IMPRINT",FACE,{"disambiguationData":[TD([[makeQuery(id+"F0.imprint","IMPRINT",EDGE,{"disambiguationData":[TD([[subQ5,1.0]])],"derivedFrom":subQ4}),-1.0]])]});}
            var Q2;
            {var subQ19=sQuery(id+"F0.wireOp",EDGE,"E46");Q2=makeQuery(id+"F0.imprint","IMPRINT",FACE,{"disambiguationData":[TD([[makeQuery(id+"F0.imprint","IMPRINT",EDGE,{"derivedFrom":subQ19}),-1.0]])]});}
            var Q3;
            Q3=makeQuery(id+"F0.imprint","IMPRINT",FACE,{"disambiguationData":[TD([[makeQuery(id+"F0.imprint","IMPRINT",EDGE,{"derivedFrom":sQuery(id+"F0.wireOp",EDGE,"E38")}),1.0]])]});
            var Q4;
            {var subQ0=sQuery(id+"F0.wireOp",EDGE,"E68");Q4=makeQuery(id+"F0.imprint","IMPRINT",FACE,{"disambiguationData":[TD([[makeQuery(id+"F0.imprint","IMPRINT",EDGE,{"derivedFrom":subQ0}),1.0]])]});}
            var Q5;
            {var subQ0=sQuery(id+"F0.wireOp",EDGE,"E92");Q5=makeQuery(id+"F0.imprint","IMPRINT",FACE,{"disambiguationData":[TD([[makeQuery(id+"F0.imprint","IMPRINT",EDGE,{"derivedFrom":subQ0}),-1.0]])]});}
            var Q6;
            {var subQ7=sQuery(id+"F0.wireOp",EDGE,"E85");Q6=makeQuery(id+"F0.imprint","IMPRINT",FACE,{"disambiguationData":[TD([[makeQuery(id+"F0.imprint","IMPRINT",EDGE,{"derivedFrom":subQ7}),1.0]])]});}
            var Q7;
            {var subQ0=sQuery(id+"F0.wireOp",EDGE,"E94");Q7=makeQuery(id+"F0.imprint","IMPRINT",FACE,{"disambiguationData":[TD([[makeQuery(id+"F0.imprint","IMPRINT",EDGE,{"derivedFrom":subQ0}),1.0]])]});}
            var Q8;
            {var subQ0=sQuery(id+"F0.wireOp",EDGE,"E99");Q8=makeQuery(id+"F0.imprint","IMPRINT",FACE,{"disambiguationData":[TD([[makeQuery(id+"F0.imprint","IMPRINT",EDGE,{"derivedFrom":subQ0}),-1.0]])]});}
            var Q9;
            {var subQ0=sQuery(id+"F0.wireOp",EDGE,"E121");Q9=makeQuery(id+"F0.imprint","IMPRINT",FACE,{"disambiguationData":[TD([[makeQuery(id+"F0.imprint","IMPRINT",EDGE,{"derivedFrom":subQ0}),1.0]])]});}
            var Q10;
            Q10=makeQuery(id+"F0.imprint","IMPRINT",FACE,{"disambiguationData":[TD([[makeQuery(id+"F0.imprint","IMPRINT",EDGE,{"derivedFrom":sQuery(id+"F0.wireOp",EDGE,"E97")}),1.0]])]});
            var Q11;
            {var subQ0=sQuery(id+"F0.wireOp",EDGE,"E135");Q11=makeQuery(id+"F0.imprint","IMPRINT",FACE,{"disambiguationData":[TD([[makeQuery(id+"F0.imprint","IMPRINT",EDGE,{"derivedFrom":subQ0}),1.0]])]});}
            var Q12;
            {var subQ0=sQuery(id+"F0.wireOp",EDGE,"E133");Q12=makeQuery(id+"F0.imprint","IMPRINT",FACE,{"disambiguationData":[TD([[makeQuery(id+"F0.imprint","IMPRINT",EDGE,{"derivedFrom":subQ0}),1.0]])]});}
            var Q13;
            {var subQ1=sQuery(id+"F0.wireOp",EDGE,"E147");Q13=makeQuery(id+"F0.imprint","IMPRINT",FACE,{"disambiguationData":[TD([[makeQuery(id+"F0.imprint","IMPRINT",EDGE,{"derivedFrom":subQ1}),1.0]])]});}
            var Q14;
            Q14=makeQuery(id+"F0.imprint","IMPRINT",FACE,{"disambiguationData":[TD([[makeQuery(id+"F0.imprint","IMPRINT",EDGE,{"derivedFrom":sQuery(id+"F0.wireOp",EDGE,"E10")}),-1.0]])]});
            extrude(context, id + "F1", {"entities" : qUnion([Q0, Q1, Q2, Q3, Q4, Q5, Q6, Q7, Q8, Q9, Q10, Q11, Q12, Q13, Q14]), "depth" : 25.4 * mm, "offsetDistance" : 25.4 * mm});
        }
        {
            var Q0;
            Q0=qCreatedBy(makeId("Top.planeOp"),FACE);
            var sketch = newSketch(context, id + "F2", { "sketchPlane" : qUnion([Q0])});
            skLineSegment(sketch, "E358.bottom", {"start": v(0, 0) * mm, "end": v(304.8, 0) * mm});
            skLineSegment(sketch, "E358.top", {"start": v(0, 304.8) * mm, "end": v(304.8, 304.8) * mm});
            skLineSegment(sketch, "E358.left", {"start": v(0, 0) * mm, "end": v(0, 304.8) * mm});
            skLineSegment(sketch, "E358.right", {"start": v(304.8, 0) * mm, "end": v(304.8, 304.8) * mm});
            skLineSegment(sketch, "E359.0", {"start": v(-25.4, 330.2) * mm, "end": v(330.2, 330.2) * mm});
            skLineSegment(sketch, "E359.1", {"start": v(-25.4, -25.4) * mm, "end": v(-25.4, 330.2) * mm});
            skLineSegment(sketch, "E359.2", {"start": v(-25.4, -25.4) * mm, "end": v(330.2, -25.4) * mm});
            skLineSegment(sketch, "E359.3", {"start": v(330.2, -25.4) * mm, "end": v(330.2, 330.2) * mm});
            skSolve(sketch);
        }
        {
            var Q0;
            Q0=makeQuery(id+"F2.imprint","IMPRINT",FACE,{"disambiguationData":[TD([[makeQuery(id+"F2.imprint","IMPRINT",EDGE,{"derivedFrom":sQuery(id+"F2.wireOp",EDGE,"E358.bottom")}),-1.0]])]});
            extrude(context, id + "F3", {"entities" : qUnion([Q0]), "depth" : 25.4 * mm, "offsetDistance" : 25.4 * mm});
        }
        {
            var Q0;
            Q0=makeQuery(id+"F1.opExtrude","CAP_FACE",FACE,{"disambiguationData":[OSD([sQuery(id+"F0.wireOp",EDGE,"E1"),sQuery(id+"F0.wireOp",EDGE,"E2"),sQuery(id+"F0.wireOp",EDGE,"E3"),sQuery(id+"F0.wireOp",EDGE,"E4"),sQuery(id+"F0.wireOp",EDGE,"E5"),sQuery(id+"F0.wireOp",EDGE,"E6"),sQuery(id+"F0.wireOp",EDGE,"E7"),sQuery(id+"F0.wireOp",EDGE,"E8"),sQuery(id+"F0.wireOp",EDGE,"E9"),sQuery(id+"F0.wireOp",EDGE,"E12"),sQuery(id+"F0.wireOp",EDGE,"E13"),sQuery(id+"F0.wireOp",EDGE,"E14"),sQuery(id+"F0.wireOp",EDGE,"E15"),sQuery(id+"F0.wireOp",EDGE,"E16"),sQuery(id+"F0.wireOp",EDGE,"E17"),sQuery(id+"F0.wireOp",EDGE,"E18"),sQuery(id+"F0.wireOp",EDGE,"E19"),sQuery(id+"F0.wireOp",EDGE,"E20"),sQuery(id+"F0.wireOp",EDGE,"E21"),sQuery(id+"F0.wireOp",EDGE,"E22"),sQuery(id+"F0.wireOp",EDGE,"E23"),sQuery(id+"F0.wireOp",EDGE,"E24"),sQuery(id+"F0.wireOp",EDGE,"E26"),sQuery(id+"F0.wireOp",EDGE,"E28"),sQuery(id+"F0.wireOp",EDGE,"E29"),sQuery(id+"F0.wireOp",EDGE,"E30"),sQuery(id+"F0.wireOp",EDGE,"E31"),sQuery(id+"F0.wireOp",EDGE,"E32"),sQuery(id+"F0.wireOp",EDGE,"E33"),sQuery(id+"F0.wireOp",EDGE,"E34"),sQuery(id+"F0.wireOp",EDGE,"E35"),sQuery(id+"F0.wireOp",EDGE,"E36"),sQuery(id+"F0.wireOp",EDGE,"E37"),sQuery(id+"F0.wireOp",EDGE,"E38"),sQuery(id+"F0.wireOp",EDGE,"E39"),sQuery(id+"F0.wireOp",EDGE,"E40"),sQuery(id+"F0.wireOp",EDGE,"E41"),sQuery(id+"F0.wireOp",EDGE,"E42"),sQuery(id+"F0.wireOp",EDGE,"E43"),sQuery(id+"F0.wireOp",EDGE,"E44"),sQuery(id+"F0.wireOp",EDGE,"E45"),sQuery(id+"F0.wireOp",EDGE,"E46"),sQuery(id+"F0.wireOp",EDGE,"E47"),sQuery(id+"F0.wireOp",EDGE,"E48"),sQuery(id+"F0.wireOp",EDGE,"E49"),sQuery(id+"F0.wireOp",EDGE,"E50"),sQuery(id+"F0.wireOp",EDGE,"E51"),sQuery(id+"F0.wireOp",EDGE,"E52"),sQuery(id+"F0.wireOp",EDGE,"E53"),sQuery(id+"F0.wireOp",EDGE,"E54"),sQuery(id+"F0.wireOp",EDGE,"E55"),sQuery(id+"F0.wireOp",EDGE,"E56"),sQuery(id+"F0.wireOp",EDGE,"E57"),sQuery(id+"F0.wireOp",EDGE,"E58"),sQuery(id+"F0.wireOp",EDGE,"E59"),sQuery(id+"F0.wireOp",EDGE,"E60"),sQuery(id+"F0.wireOp",EDGE,"E61"),sQuery(id+"F0.wireOp",EDGE,"E62"),sQuery(id+"F0.wireOp",EDGE,"E63"),sQuery(id+"F0.wireOp",EDGE,"E64"),sQuery(id+"F0.wireOp",EDGE,"E65"),sQuery(id+"F0.wireOp",EDGE,"E66"),sQuery(id+"F0.wireOp",EDGE,"E67"),sQuery(id+"F0.wireOp",EDGE,"E68"),sQuery(id+"F0.wireOp",EDGE,"E69"),sQuery(id+"F0.wireOp",EDGE,"E70"),sQuery(id+"F0.wireOp",EDGE,"E71"),sQuery(id+"F0.wireOp",EDGE,"E72"),sQuery(id+"F0.wireOp",EDGE,"E73"),sQuery(id+"F0.wireOp",EDGE,"E74"),sQuery(id+"F0.wireOp",EDGE,"E75"),sQuery(id+"F0.wireOp",EDGE,"E76"),sQuery(id+"F0.wireOp",EDGE,"E77"),sQuery(id+"F0.wireOp",EDGE,"E78"),sQuery(id+"F0.wireOp",EDGE,"E79"),sQuery(id+"F0.wireOp",EDGE,"E80"),sQuery(id+"F0.wireOp",EDGE,"E81"),sQuery(id+"F0.wireOp",EDGE,"E82"),sQuery(id+"F0.wireOp",EDGE,"E83"),sQuery(id+"F0.wireOp",EDGE,"E84"),sQuery(id+"F0.wireOp",EDGE,"E85"),sQuery(id+"F0.wireOp",EDGE,"E86"),sQuery(id+"F0.wireOp",EDGE,"E87"),sQuery(id+"F0.wireOp",EDGE,"E88"),sQuery(id+"F0.wireOp",EDGE,"E89"),sQuery(id+"F0.wireOp",EDGE,"E90"),sQuery(id+"F0.wireOp",EDGE,"E91"),sQuery(id+"F0.wireOp",EDGE,"E92"),sQuery(id+"F0.wireOp",EDGE,"E93"),sQuery(id+"F0.wireOp",EDGE,"E94"),sQuery(id+"F0.wireOp",EDGE,"E95"),sQuery(id+"F0.wireOp",EDGE,"E96"),sQuery(id+"F0.wireOp",EDGE,"E97"),sQuery(id+"F0.wireOp",EDGE,"E98"),sQuery(id+"F0.wireOp",EDGE,"E99"),sQuery(id+"F0.wireOp",EDGE,"E100"),sQuery(id+"F0.wireOp",EDGE,"E101"),sQuery(id+"F0.wireOp",EDGE,"E102"),sQuery(id+"F0.wireOp",EDGE,"E103"),sQuery(id+"F0.wireOp",EDGE,"E104"),sQuery(id+"F0.wireOp",EDGE,"E105"),sQuery(id+"F0.wireOp",EDGE,"E106"),sQuery(id+"F0.wireOp",EDGE,"E107"),sQuery(id+"F0.wireOp",EDGE,"E108"),sQuery(id+"F0.wireOp",EDGE,"E109"),sQuery(id+"F0.wireOp",EDGE,"E110"),sQuery(id+"F0.wireOp",EDGE,"E111"),sQuery(id+"F0.wireOp",EDGE,"E112"),sQuery(id+"F0.wireOp",EDGE,"E113"),sQuery(id+"F0.wireOp",EDGE,"E114"),sQuery(id+"F0.wireOp",EDGE,"E115"),sQuery(id+"F0.wireOp",EDGE,"E116"),sQuery(id+"F0.wireOp",EDGE,"E117"),sQuery(id+"F0.wireOp",EDGE,"E118"),sQuery(id+"F0.wireOp",EDGE,"E119"),sQuery(id+"F0.wireOp",EDGE,"E120"),sQuery(id+"F0.wireOp",EDGE,"E121"),sQuery(id+"F0.wireOp",EDGE,"E122"),sQuery(id+"F0.wireOp",EDGE,"E125"),sQuery(id+"F0.wireOp",EDGE,"E126"),sQuery(id+"F0.wireOp",EDGE,"E127"),sQuery(id+"F0.wireOp",EDGE,"E128"),sQuery(id+"F0.wireOp",EDGE,"E129"),sQuery(id+"F0.wireOp",EDGE,"E130"),sQuery(id+"F0.wireOp",EDGE,"E131"),sQuery(id+"F0.wireOp",EDGE,"E132"),sQuery(id+"F0.wireOp",EDGE,"E133"),sQuery(id+"F0.wireOp",EDGE,"E134"),sQuery(id+"F0.wireOp",EDGE,"E135"),sQuery(id+"F0.wireOp",EDGE,"E136"),sQuery(id+"F0.wireOp",EDGE,"E137"),sQuery(id+"F0.wireOp",EDGE,"E138"),sQuery(id+"F0.wireOp",EDGE,"E139"),sQuery(id+"F0.wireOp",EDGE,"E140"),sQuery(id+"F0.wireOp",EDGE,"E141"),sQuery(id+"F0.wireOp",EDGE,"E142"),sQuery(id+"F0.wireOp",EDGE,"E143"),sQuery(id+"F0.wireOp",EDGE,"E144"),sQuery(id+"F0.wireOp",EDGE,"E145"),sQuery(id+"F0.wireOp",EDGE,"E146"),sQuery(id+"F0.wireOp",EDGE,"E147"),sQuery(id+"F0.wireOp",EDGE,"E148"),sQuery(id+"F0.wireOp",EDGE,"E149"),sQuery(id+"F0.wireOp",EDGE,"E150"),sQuery(id+"F0.wireOp",EDGE,"E151.trimOffspring"),sQuery(id+"F0.wireOp",EDGE,"E152"),sQuery(id+"F0.wireOp",EDGE,"E153"),sQuery(id+"F0.wireOp",EDGE,"E154"),sQuery(id+"F0.wireOp",EDGE,"E155"),sQuery(id+"F0.wireOp",EDGE,"E156"),sQuery(id+"F0.wireOp",EDGE,"E157"),sQuery(id+"F0.wireOp",EDGE,"E158"),sQuery(id+"F0.wireOp",EDGE,"E161"),sQuery(id+"F0.wireOp",EDGE,"E162"),sQuery(id+"F0.wireOp",EDGE,"E163"),sQuery(id+"F0.wireOp",EDGE,"E164"),sQuery(id+"F0.wireOp",EDGE,"E165"),sQuery(id+"F0.wireOp",EDGE,"E166"),sQuery(id+"F0.wireOp",EDGE,"E167"),sQuery(id+"F0.wireOp",EDGE,"E168"),sQuery(id+"F0.wireOp",EDGE,"E169"),sQuery(id+"F0.wireOp",EDGE,"E170"),sQuery(id+"F0.wireOp",EDGE,"E171"),sQuery(id+"F0.wireOp",EDGE,"E172"),sQuery(id+"F0.wireOp",EDGE,"E173"),sQuery(id+"F0.wireOp",EDGE,"E174"),sQuery(id+"F0.wireOp",EDGE,"E175"),sQuery(id+"F0.wireOp",EDGE,"E176"),sQuery(id+"F0.wireOp",EDGE,"E177"),sQuery(id+"F0.wireOp",EDGE,"E178"),sQuery(id+"F0.wireOp",EDGE,"E179"),sQuery(id+"F0.wireOp",EDGE,"E180"),sQuery(id+"F0.wireOp",EDGE,"E181"),sQuery(id+"F0.wireOp",EDGE,"E182"),sQuery(id+"F0.wireOp",EDGE,"E183"),sQuery(id+"F0.wireOp",EDGE,"E184"),sQuery(id+"F0.wireOp",EDGE,"E185"),sQuery(id+"F0.wireOp",EDGE,"E186"),sQuery(id+"F0.wireOp",EDGE,"E187"),sQuery(id+"F0.wireOp",EDGE,"E188"),sQuery(id+"F0.wireOp",EDGE,"E189"),sQuery(id+"F0.wireOp",EDGE,"E190"),sQuery(id+"F0.wireOp",EDGE,"E191"),sQuery(id+"F0.wireOp",EDGE,"E192"),sQuery(id+"F0.wireOp",EDGE,"E193"),sQuery(id+"F0.wireOp",EDGE,"E194"),sQuery(id+"F0.wireOp",EDGE,"E195"),sQuery(id+"F0.wireOp",EDGE,"E196"),sQuery(id+"F0.wireOp",EDGE,"E197"),sQuery(id+"F0.wireOp",EDGE,"E198"),sQuery(id+"F0.wireOp",EDGE,"E199"),sQuery(id+"F0.wireOp",EDGE,"E200"),sQuery(id+"F0.wireOp",EDGE,"E201"),sQuery(id+"F0.wireOp",EDGE,"E202"),sQuery(id+"F0.wireOp",EDGE,"E203"),sQuery(id+"F0.wireOp",EDGE,"E204"),sQuery(id+"F0.wireOp",EDGE,"E205"),sQuery(id+"F0.wireOp",EDGE,"E206"),sQuery(id+"F0.wireOp",EDGE,"E207"),sQuery(id+"F0.wireOp",EDGE,"E208"),sQuery(id+"F0.wireOp",EDGE,"E209"),sQuery(id+"F0.wireOp",EDGE,"E210"),sQuery(id+"F0.wireOp",EDGE,"E211"),sQuery(id+"F0.wireOp",EDGE,"E212"),sQuery(id+"F0.wireOp",EDGE,"E213"),sQuery(id+"F0.wireOp",EDGE,"E214"),sQuery(id+"F0.wireOp",EDGE,"E216"),sQuery(id+"F0.wireOp",EDGE,"E217"),sQuery(id+"F0.wireOp",EDGE,"E218"),sQuery(id+"F0.wireOp",EDGE,"E219"),sQuery(id+"F0.wireOp",EDGE,"E220"),sQuery(id+"F0.wireOp",EDGE,"E221"),sQuery(id+"F0.wireOp",EDGE,"E222"),sQuery(id+"F0.wireOp",EDGE,"E223"),sQuery(id+"F0.wireOp",EDGE,"E228"),sQuery(id+"F0.wireOp",EDGE,"E229"),sQuery(id+"F0.wireOp",EDGE,"E230"),sQuery(id+"F0.wireOp",EDGE,"E231"),sQuery(id+"F0.wireOp",EDGE,"E232"),sQuery(id+"F0.wireOp",EDGE,"E233"),sQuery(id+"F0.wireOp",EDGE,"E234"),sQuery(id+"F0.wireOp",EDGE,"E235"),sQuery(id+"F0.wireOp",EDGE,"E236"),sQuery(id+"F0.wireOp",EDGE,"E237"),sQuery(id+"F0.wireOp",EDGE,"E238"),sQuery(id+"F0.wireOp",EDGE,"E239"),sQuery(id+"F0.wireOp",EDGE,"E240.0"),sQuery(id+"F0.wireOp",EDGE,"E241.0"),sQuery(id+"F0.wireOp",EDGE,"E242.0"),sQuery(id+"F0.wireOp",EDGE,"E243.0"),sQuery(id+"F0.wireOp",EDGE,"E244.0"),sQuery(id+"F0.wireOp",EDGE,"E245"),sQuery(id+"F0.wireOp",EDGE,"E246"),sQuery(id+"F0.wireOp",EDGE,"E247"),sQuery(id+"F0.wireOp",EDGE,"E248"),sQuery(id+"F0.wireOp",EDGE,"E249"),sQuery(id+"F0.wireOp",EDGE,"E250"),sQuery(id+"F0.wireOp",EDGE,"E251"),sQuery(id+"F0.wireOp",EDGE,"E252"),sQuery(id+"F0.wireOp",EDGE,"E253"),sQuery(id+"F0.wireOp",EDGE,"E254"),sQuery(id+"F0.wireOp",EDGE,"E255.0"),sQuery(id+"F0.wireOp",EDGE,"E256"),sQuery(id+"F0.wireOp",EDGE,"E257"),sQuery(id+"F0.wireOp",EDGE,"E258"),sQuery(id+"F0.wireOp",EDGE,"E259"),sQuery(id+"F0.wireOp",EDGE,"E260"),sQuery(id+"F0.wireOp",EDGE,"E261"),sQuery(id+"F0.wireOp",EDGE,"E262"),sQuery(id+"F0.wireOp",EDGE,"E263"),sQuery(id+"F0.wireOp",EDGE,"E264"),sQuery(id+"F0.wireOp",EDGE,"E265"),sQuery(id+"F0.wireOp",EDGE,"E266"),sQuery(id+"F0.wireOp",EDGE,"E267"),sQuery(id+"F0.wireOp",EDGE,"E268"),sQuery(id+"F0.wireOp",EDGE,"E269"),sQuery(id+"F0.wireOp",EDGE,"E270"),sQuery(id+"F0.wireOp",EDGE,"E271"),sQuery(id+"F0.wireOp",EDGE,"E272"),sQuery(id+"F0.wireOp",EDGE,"E273"),sQuery(id+"F0.wireOp",EDGE,"E274"),sQuery(id+"F0.wireOp",EDGE,"E275"),sQuery(id+"F0.wireOp",EDGE,"E276"),sQuery(id+"F0.wireOp",EDGE,"E277"),sQuery(id+"F0.wireOp",EDGE,"E278"),sQuery(id+"F0.wireOp",EDGE,"E279"),sQuery(id+"F0.wireOp",EDGE,"E280"),sQuery(id+"F0.wireOp",EDGE,"E281"),sQuery(id+"F0.wireOp",EDGE,"E282"),sQuery(id+"F0.wireOp",EDGE,"E283"),sQuery(id+"F0.wireOp",EDGE,"E284"),sQuery(id+"F0.wireOp",EDGE,"E285"),sQuery(id+"F0.wireOp",EDGE,"E286"),sQuery(id+"F0.wireOp",EDGE,"E287"),sQuery(id+"F0.wireOp",EDGE,"E288"),sQuery(id+"F0.wireOp",EDGE,"E289"),sQuery(id+"F0.wireOp",EDGE,"E290"),sQuery(id+"F0.wireOp",EDGE,"E291"),sQuery(id+"F0.wireOp",EDGE,"E292"),sQuery(id+"F0.wireOp",EDGE,"E293"),sQuery(id+"F0.wireOp",EDGE,"E294"),sQuery(id+"F0.wireOp",EDGE,"E295"),sQuery(id+"F0.wireOp",EDGE,"E296"),sQuery(id+"F0.wireOp",EDGE,"E297"),sQuery(id+"F0.wireOp",EDGE,"E298"),sQuery(id+"F0.wireOp",EDGE,"E299"),sQuery(id+"F0.wireOp",EDGE,"E300"),sQuery(id+"F0.wireOp",EDGE,"E301"),sQuery(id+"F0.wireOp",EDGE,"E302"),sQuery(id+"F0.wireOp",EDGE,"E303"),sQuery(id+"F0.wireOp",EDGE,"E304"),sQuery(id+"F0.wireOp",EDGE,"E305"),sQuery(id+"F0.wireOp",EDGE,"E307.trimOffspring"),sQuery(id+"F0.wireOp",EDGE,"E308.trimOffspring"),sQuery(id+"F0.wireOp",EDGE,"E309.trimOffspring"),sQuery(id+"F0.wireOp",EDGE,"E310.trimOffspring"),sQuery(id+"F0.wireOp",EDGE,"E311.trimOffspring"),sQuery(id+"F0.wireOp",EDGE,"E312.trimOffspring"),sQuery(id+"F0.wireOp",EDGE,"E313.trimOffspring"),sQuery(id+"F0.wireOp",EDGE,"E314.trimOffspring"),sQuery(id+"F0.wireOp",EDGE,"E315.trimOffspring"),sQuery(id+"F0.wireOp",EDGE,"E316.trimOffspring"),sQuery(id+"F0.wireOp",EDGE,"E317.trimOffspring"),sQuery(id+"F0.wireOp",EDGE,"E318.trimOffspring"),sQuery(id+"F0.wireOp",EDGE,"E319.trimOffspring"),sQuery(id+"F0.wireOp",EDGE,"E320.trimOffspring"),sQuery(id+"F0.wireOp",EDGE,"E321.trimOffspring"),sQuery(id+"F0.wireOp",EDGE,"E322.trimOffspring"),sQuery(id+"F0.wireOp",EDGE,"E323.trimOffspring"),sQuery(id+"F0.wireOp",EDGE,"E324.trimOffspring"),sQuery(id+"F0.wireOp",EDGE,"E325.trimOffspring"),sQuery(id+"F0.wireOp",EDGE,"E326.trimOffspring"),sQuery(id+"F0.wireOp",EDGE,"E327.trimOffspring"),sQuery(id+"F0.wireOp",EDGE,"E328.trimOffspring"),sQuery(id+"F0.wireOp",EDGE,"E329.trimOffspring"),sQuery(id+"F0.wireOp",EDGE,"E330.trimOffspring"),sQuery(id+"F0.wireOp",EDGE,"E331"),sQuery(id+"F0.wireOp",EDGE,"E332.trimOffspring"),sQuery(id+"F0.wireOp",EDGE,"E334.extension"),sQuery(id+"F0.wireOp",EDGE,"E335.trimOffspring"),sQuery(id+"F0.wireOp",EDGE,"E336.trimOffspring"),sQuery(id+"F0.wireOp",EDGE,"E337.trimOffspring"),sQuery(id+"F0.wireOp",EDGE,"E338.trimOffspring"),sQuery(id+"F0.wireOp",EDGE,"E339.trimOffspring"),sQuery(id+"F0.wireOp",EDGE,"E340.trimOffspring"),sQuery(id+"F0.wireOp",EDGE,"E341.trimOffspring"),sQuery(id+"F0.wireOp",EDGE,"E342.trimOffspring"),sQuery(id+"F0.wireOp",EDGE,"E343.trimOffspring"),sQuery(id+"F0.wireOp",EDGE,"E345.trimOffspring"),sQuery(id+"F0.wireOp",EDGE,"E346.trimOffspring"),sQuery(id+"F0.wireOp",EDGE,"E347.trimOffspring"),sQuery(id+"F0.wireOp",EDGE,"E348.trimOffspring"),sQuery(id+"F0.wireOp",EDGE,"E349"),sQuery(id+"F0.wireOp",EDGE,"E351"),sQuery(id+"F0.wireOp",EDGE,"E354.bottom"),sQuery(id+"F0.wireOp",EDGE,"E354.left"),sQuery(id+"F0.wireOp",EDGE,"E355"),sQuery(id+"F0.wireOp",EDGE,"E356"),sQuery(id+"F0.wireOp",EDGE,"E357")])],"isStart":false});
            var sketch = newSketch(context, id + "F4", { "sketchPlane" : qUnion([Q0])});
            skLineSegment(sketch, "E360.0", {"start": v(0, 0) * mm, "end": v(304.8, 0) * mm});
            skPoint(sketch, "E361.0", {"position": v(240.22, -30.41) * mm});
            skLineSegment(sketch, "E362.0", {"start": v(330.2, 330.2) * mm, "end": v(330.2, -25.4) * mm});
            skLineSegment(sketch, "E363.0", {"start": v(-25.4, 330.2) * mm, "end": v(330.2, 330.2) * mm});
            skLineSegment(sketch, "E364.0", {"start": v(-25.4, 330.2) * mm, "end": v(-25.4, -25.4) * mm});
            skPoint(sketch, "E365.0.end.orphan", {"position": v(304.8, 304.8) * mm});
            skPoint(sketch, "E365.0.start.orphan", {"position": v(0, 304.8) * mm});
            skLineSegment(sketch, "E366", {"start": v(221.94, 304.8) * mm, "end": v(304.8, 304.8) * mm});
            skLineSegment(sketch, "E367", {"start": v(212.83, 304.8) * mm, "end": v(188.16, 304.8) * mm});
            skLineSegment(sketch, "E368", {"start": v(185.1, 304.78) * mm, "end": v(0, 304.8) * mm});
            skPoint(sketch, "E369.0.end.orphan", {"position": v(304.8, 0) * mm});
            skLineSegment(sketch, "E370", {"start": v(304.8, 88.22) * mm, "end": v(304.8, 253.65) * mm});
            skLineSegment(sketch, "E371", {"start": v(304.8, 278.4) * mm, "end": v(304.8, 304.8) * mm});
            skLineSegment(sketch, "E372", {"start": v(304.8, 72.01) * mm, "end": v(304.8, 0) * mm});
            skPoint(sketch, "E373.0.end.orphan", {"position": v(0, 0) * mm});
            skLineSegment(sketch, "E374", {"start": v(0, 0) * mm, "end": v(0, 69.4) * mm});
            skLineSegment(sketch, "E375", {"start": v(0.01, 78.06) * mm, "end": v(0, 304.8) * mm});
            skSolve(sketch);
        }
        {
            var Q0;
            Q0=makeQuery(id+"F4.imprint","IMPRINT",FACE,{"disambiguationData":[TD([[makeQuery(id+"F4.imprint","IMPRINT",EDGE,{"derivedFrom":makeQuery(id+"F1.opExtrude","CAP_EDGE",EDGE,{"disambiguationData":[OSD([sQuery(id+"F0.wireOp",EDGE,"E1")])],"isStart":false})}),1.0]])]});
            var Q1;
            Q1=makeQuery(id+"F3.opExtrude","CAP_FACE",FACE,{"disambiguationData":[OSD([sQuery(id+"F2.wireOp",EDGE,"E358.bottom"),sQuery(id+"F2.wireOp",EDGE,"E358.top"),sQuery(id+"F2.wireOp",EDGE,"E358.left"),sQuery(id+"F2.wireOp",EDGE,"E358.right"),sQuery(id+"F2.wireOp",EDGE,"E359.0"),sQuery(id+"F2.wireOp",EDGE,"E359.1"),sQuery(id+"F2.wireOp",EDGE,"E359.2"),sQuery(id+"F2.wireOp",EDGE,"E359.3")])],"isStart":false});
            extrude(context, id + "F5", {"entities" : qUnion([Q0, Q1]), "depth" : 25.4 * mm, "offsetDistance" : 25.4 * mm});
        }
    });
